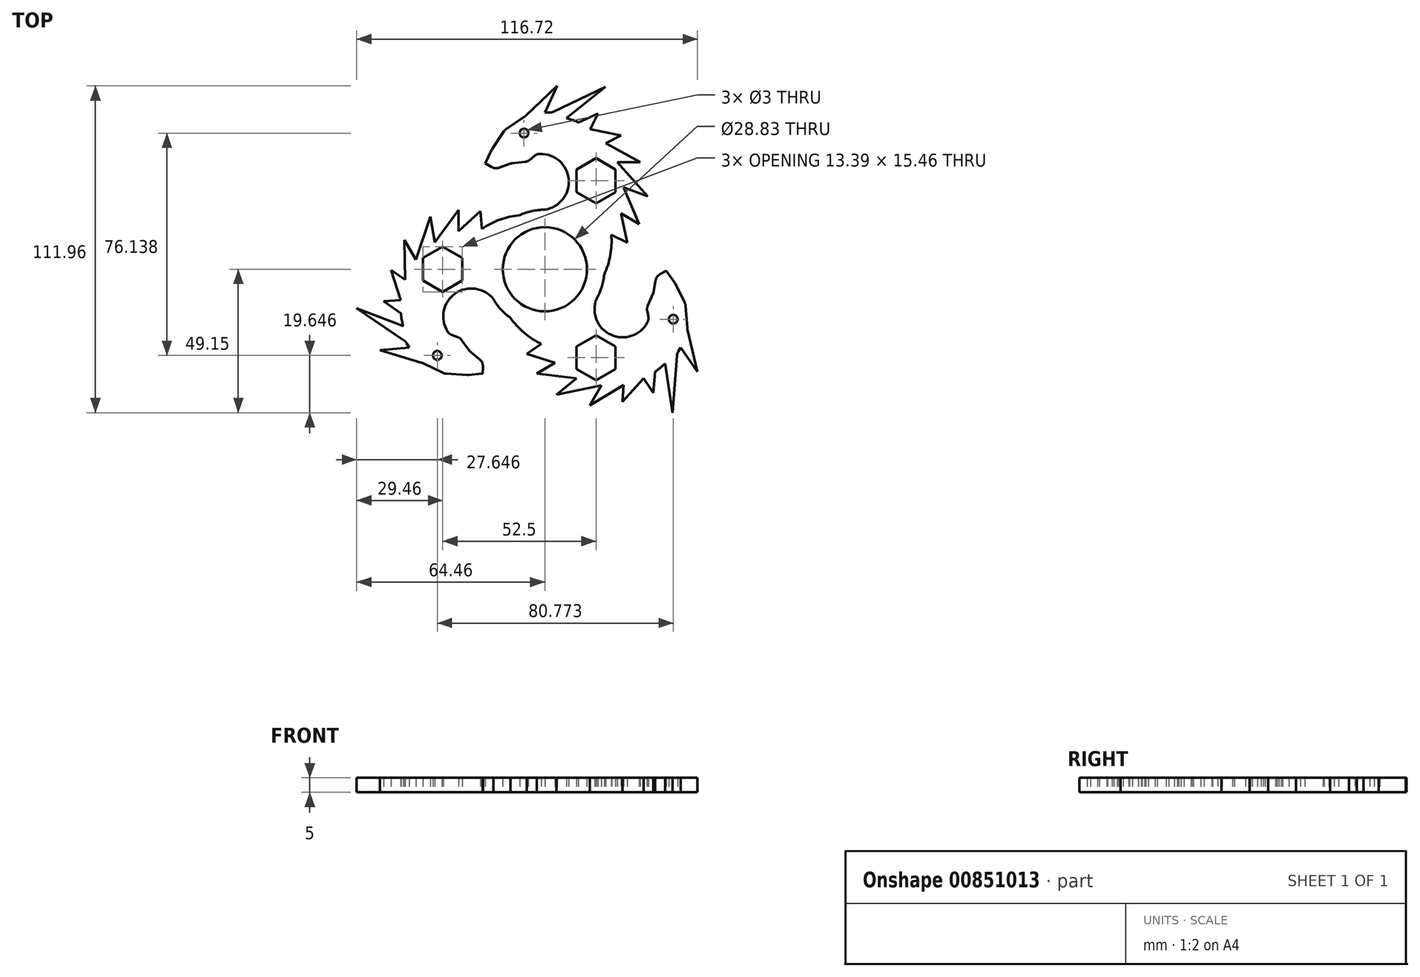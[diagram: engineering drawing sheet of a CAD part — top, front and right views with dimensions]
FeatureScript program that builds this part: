
annotation { "Feature Type Name" : "Feature", "Feature Type Description" : "" }
export const myFeature = defineFeature(function(context is Context, id is Id, definition is map)
    precondition{}
    {
        {
            var Q0;
            Q0=qCreatedBy(makeId("Top.planeOp"),FACE);
            var sketch = newSketch(context, id + "F0", { "sketchPlane" : qUnion([Q0])});
            skArc(sketch, "E0", {"start": v(0, 20.4) * mm, "mid": v(8.14, 30.78) * mm, "end": v(-1.75, 39.51) * mm});
            skLineSegment(sketch, "E1", {"start": v(7.42, 51.76) * mm, "end": v(20.67, 62.5) * mm});
            skLineSegment(sketch, "E2", {"start": v(20.67, 62.5) * mm, "end": v(2.99, 53.95) * mm});
            skLineSegment(sketch, "E3", {"start": v(1.68, 53.66) * mm, "end": v(0, 53.66) * mm});
            skLineSegment(sketch, "E4", {"start": v(-6.98, 52.26) * mm, "end": v(-13.25, 47.99) * mm});
            skLineSegment(sketch, "E5", {"start": v(-20.36, 36.3) * mm, "end": v(-18.24, 40.82) * mm});
            skLineSegment(sketch, "E6", {"start": v(-18.02, 41.22) * mm, "end": v(-14.05, 47.17) * mm});
            skLineSegment(sketch, "E7", {"start": v(-3.58, 38.81) * mm, "end": v(-5.17, 37.47) * mm});
            skLineSegment(sketch, "E8", {"start": v(-6.77, 36.79) * mm, "end": v(-11.2, 36.3) * mm});
            skLineSegment(sketch, "E9", {"start": v(-11.89, 36.13) * mm, "end": v(-15.65, 34.77) * mm});
            skLineSegment(sketch, "E10", {"start": v(-18.22, 35.01) * mm, "end": v(-20.36, 36.3) * mm});
            skLineSegment(sketch, "E11", {"start": v(0, 53.66) * mm, "end": v(4.26, 62.8) * mm});
            skLineSegment(sketch, "E12", {"start": v(4.26, 62.8) * mm, "end": v(-6.61, 52.56) * mm});
            skLineSegment(sketch, "E13", {"start": v(15.49, 48.02) * mm, "end": v(26.04, 45.77) * mm});
            skLineSegment(sketch, "E14", {"start": v(26.04, 45.77) * mm, "end": v(20.8, 43.18) * mm});
            skLineSegment(sketch, "E15", {"start": v(20.8, 43.18) * mm, "end": v(32.67, 36.61) * mm});
            skLineSegment(sketch, "E16", {"start": v(32.67, 36.61) * mm, "end": v(24.84, 36.61) * mm});
            skLineSegment(sketch, "E17", {"start": v(24.84, 36.61) * mm, "end": v(35.2, 24.93) * mm});
            skLineSegment(sketch, "E18", {"start": v(35.2, 24.93) * mm, "end": v(26.92, 28.04) * mm});
            skLineSegment(sketch, "E19", {"start": v(26.92, 28.04) * mm, "end": v(32.35, 15.47) * mm});
            skLineSegment(sketch, "E20", {"start": v(32.35, 15.47) * mm, "end": v(26.04, 19.1) * mm});
            skLineSegment(sketch, "E21", {"start": v(26.04, 19.1) * mm, "end": v(28.25, 9.15) * mm});
            skLineSegment(sketch, "E22", {"start": v(28.25, 9.15) * mm, "end": v(22.76, 11.77) * mm});
            skLineSegment(sketch, "E23", {"start": v(11.52, 50.27) * mm, "end": v(18.15, 53.34) * mm});
            skPoint(sketch, "E23.startSnap0", {"position": v(11.52, 58.07) * mm});
            skLineSegment(sketch, "E24", {"start": v(18.15, 53.34) * mm, "end": v(15.49, 48.02) * mm});
            skPoint(sketch, "E25.visualSharp", {"position": v(-17, 34.28) * mm});
            skArc(sketch, "E25.filletArc", {"start": v(-18.22, 35.01) * mm, "mid": v(-16.96, 34.6) * mm, "end": v(-15.65, 34.77) * mm});
            skPoint(sketch, "E26.visualSharp", {"position": v(-11.55, 36.26) * mm});
            skArc(sketch, "E26.filletArc", {"start": v(-11.2, 36.3) * mm, "mid": v(-11.54, 36.24) * mm, "end": v(-11.89, 36.13) * mm});
            skPoint(sketch, "E27.visualSharp", {"position": v(-5.87, 36.89) * mm});
            skArc(sketch, "E27.filletArc", {"start": v(-6.77, 36.79) * mm, "mid": v(-5.92, 37.01) * mm, "end": v(-5.17, 37.47) * mm});
            skPoint(sketch, "E28.visualSharp", {"position": v(-2.87, 39.41) * mm});
            skArc(sketch, "E28.filletArc", {"start": v(-1.75, 39.51) * mm, "mid": v(-2.72, 39.32) * mm, "end": v(-3.58, 38.81) * mm});
            skPoint(sketch, "E29.visualSharp", {"position": v(-18.15, 41.03) * mm});
            skArc(sketch, "E29.filletArc", {"start": v(-18.02, 41.22) * mm, "mid": v(-18.14, 41.03) * mm, "end": v(-18.24, 40.82) * mm});
            skPoint(sketch, "E30.visualSharp", {"position": v(-13.73, 47.66) * mm});
            skArc(sketch, "E30.filletArc", {"start": v(-13.25, 47.99) * mm, "mid": v(-13.69, 47.62) * mm, "end": v(-14.05, 47.17) * mm});
            skPoint(sketch, "E31.visualSharp", {"position": v(-6.79, 52.4) * mm});
            skArc(sketch, "E31.filletArc", {"start": v(-6.98, 52.26) * mm, "mid": v(-6.8, 52.4) * mm, "end": v(-6.61, 52.56) * mm});
            skPoint(sketch, "E32.visualSharp", {"position": v(2.37, 53.66) * mm});
            skArc(sketch, "E32.filletArc", {"start": v(1.68, 53.66) * mm, "mid": v(2.35, 53.73) * mm, "end": v(2.99, 53.95) * mm});
            skArc(sketch, "E33", {"start": v(20.32, -1.85) * mm, "mid": v(22.4, 4.8) * mm, "end": v(22.76, 11.77) * mm});
            skArc(sketch, "E34.trimOffspring", {"start": v(11.52, 50.27) * mm, "mid": v(9.5, 51.1) * mm, "end": v(7.42, 51.76) * mm});
            skArc(sketch, "E35", {"start": v(20.32, -1.85) * mm, "mid": v(19.45, -6.17) * mm, "end": v(17.67, -10.2) * mm});
            skArc(sketch, "E36", {"start": v(0, 14.42) * mm, "mid": v(12.48, 7.2) * mm, "end": v(12.48, -7.2) * mm});
            skLineSegment(sketch, "E37", {"start": v(0, 0) * mm, "end": v(40.8, 0) * mm, "construction": true});
            skLineSegment(sketch, "E38", {"start": v(0, 0) * mm, "end": v(17.5, 30.31) * mm, "construction": true});
            skCircle(sketch, "E39", {"center": v(-7.14, 46.63) * mm, "radius": 1.5 * mm});
            skLineSegment(sketch, "E40", {"start": v(12.48, -7.2) * mm, "end": v(17.67, -10.2) * mm});
            skLineSegment(sketch, "E41", {"start": v(0, 20.4) * mm, "end": v(0, 14.42) * mm});
            skCircle(sketch, "E42.cCircle", {"center": v(17.5, 30.31) * mm, "radius": 7.73 * mm, "construction": true});
            skLineSegment(sketch, "E42.0", {"start": v(17.5, 38.04) * mm, "end": v(24.2, 34.18) * mm});
            skLineSegment(sketch, "E42.1", {"start": v(24.2, 34.18) * mm, "end": v(24.2, 26.44) * mm});
            skLineSegment(sketch, "E42.2", {"start": v(24.2, 26.44) * mm, "end": v(17.5, 22.58) * mm});
            skLineSegment(sketch, "E42.3", {"start": v(17.5, 22.58) * mm, "end": v(10.8, 26.44) * mm});
            skLineSegment(sketch, "E42.4", {"start": v(10.8, 26.44) * mm, "end": v(10.8, 34.18) * mm});
            skLineSegment(sketch, "E42.5", {"start": v(10.8, 34.18) * mm, "end": v(17.5, 38.04) * mm});
            skSolve(sketch);
        }
        {
            var Q0;
            Q0=makeQuery(id+"F0.imprint","IMPRINT",FACE,{"disambiguationData":[TD([[makeQuery(id+"F0.imprint","IMPRINT",EDGE,{"derivedFrom":sQuery(id+"F0.wireOp",EDGE,"ab7987d0-8e88-4c48-aa86-221078aa2c68")}),1.0]])]});
            var Q1;
            Q1=makeQuery(id+"F0.imprint","IMPRINT",FACE,{"disambiguationData":[TD([[makeQuery(id+"F0.imprint","IMPRINT",EDGE,{"derivedFrom":sQuery(id+"F0.wireOp",EDGE,"E0")}),-1.0]])]});
            extrude(context, id + "F1", {"entities" : qUnion([Q0, Q1]), "depth" : 5 * mm, "offsetDistance" : 25 * mm});
        }
        {
            var Q0;
            Q0=qCreatedBy(makeId("Front.planeOp"),FACE);
            var sketch = newSketch(context, id + "F2", { "sketchPlane" : qUnion([Q0])});
            skLineSegment(sketch, "E43", {"start": v(0, 0) * mm, "end": v(0, 43.66) * mm});
            skSolve(sketch);
        }
        {
            var Q0;
            Q0=makeQuery(id+"F1.opExtrude","SWEPT_BODY",BODY,{"disambiguationData":[OSD([sQuery(id+"F0.wireOp",EDGE,"ab7987d0-8e88-4c48-aa86-221078aa2c68"),sQuery(id+"F0.wireOp",EDGE,"E0"),sQuery(id+"F0.wireOp",EDGE,"E1"),sQuery(id+"F0.wireOp",EDGE,"E2"),sQuery(id+"F0.wireOp",EDGE,"E3"),sQuery(id+"F0.wireOp",EDGE,"E4"),sQuery(id+"F0.wireOp",EDGE,"E5"),sQuery(id+"F0.wireOp",EDGE,"E6"),sQuery(id+"F0.wireOp",EDGE,"E7"),sQuery(id+"F0.wireOp",EDGE,"E8"),sQuery(id+"F0.wireOp",EDGE,"E9"),sQuery(id+"F0.wireOp",EDGE,"E10"),sQuery(id+"F0.wireOp",EDGE,"E11"),sQuery(id+"F0.wireOp",EDGE,"E12"),sQuery(id+"F0.wireOp",EDGE,"E13"),sQuery(id+"F0.wireOp",EDGE,"E14"),sQuery(id+"F0.wireOp",EDGE,"E15"),sQuery(id+"F0.wireOp",EDGE,"E16"),sQuery(id+"F0.wireOp",EDGE,"E17"),sQuery(id+"F0.wireOp",EDGE,"E18"),sQuery(id+"F0.wireOp",EDGE,"E19"),sQuery(id+"F0.wireOp",EDGE,"E20"),sQuery(id+"F0.wireOp",EDGE,"E21"),sQuery(id+"F0.wireOp",EDGE,"E22"),sQuery(id+"F0.wireOp",EDGE,"E23"),sQuery(id+"F0.wireOp",EDGE,"E24"),sQuery(id+"F0.wireOp",EDGE,"E25.filletArc"),sQuery(id+"F0.wireOp",EDGE,"E26.filletArc"),sQuery(id+"F0.wireOp",EDGE,"E27.filletArc"),sQuery(id+"F0.wireOp",EDGE,"E28.filletArc"),sQuery(id+"F0.wireOp",EDGE,"E29.filletArc"),sQuery(id+"F0.wireOp",EDGE,"E30.filletArc"),sQuery(id+"F0.wireOp",EDGE,"E31.filletArc"),sQuery(id+"F0.wireOp",EDGE,"E32.filletArc"),sQuery(id+"F0.wireOp",EDGE,"E33"),sQuery(id+"F0.wireOp",EDGE,"E34.trimOffspring")])]});
            var Q1;
            Q1=sQuery(id+"F2.wireOp",EDGE,"E43");
            circularPattern(context, id + "F3", {"operationType" : NewBodyOperationType.ADD, "entities" : qUnion([Q0]), "axis" : qUnion([Q1]), "angle" : 360 * degree, "instanceCount" : 3, "equalSpace" : true});
        }
    });
